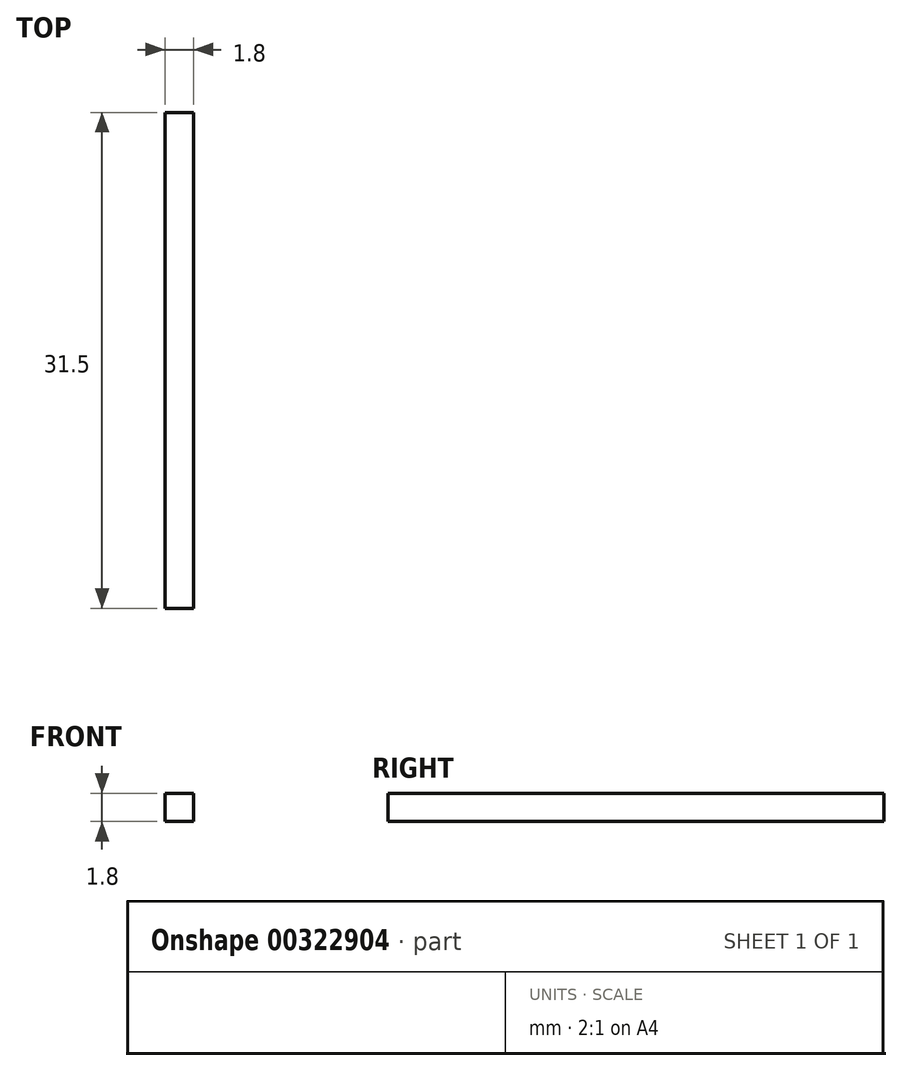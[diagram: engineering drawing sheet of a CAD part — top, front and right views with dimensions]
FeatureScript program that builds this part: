
annotation { "Feature Type Name" : "Feature", "Feature Type Description" : "" }
export const myFeature = defineFeature(function(context is Context, id is Id, definition is map)
    precondition{}
    {
        {
            var Q0;
            Q0=qCreatedBy(makeId("Front.planeOp"),FACE);
            var sketch = newSketch(context, id + "F0", { "sketchPlane" : qUnion([Q0])});
            skLineSegment(sketch, "E0.bottom", {"start": v(2.38, 2.38) * mm, "end": v(-2.37, 2.38) * mm});
            skLineSegment(sketch, "E0.top", {"start": v(2.37, -2.37) * mm, "end": v(-2.38, -2.37) * mm});
            skLineSegment(sketch, "E0.left", {"start": v(2.38, 2.38) * mm, "end": v(2.37, -2.37) * mm});
            skLineSegment(sketch, "E0.right", {"start": v(-2.37, 2.38) * mm, "end": v(-2.38, -2.37) * mm});
            skPoint(sketch, "E0.middle", {"position": v(0, 0) * mm});
            skLineSegment(sketch, "E1.bottom", {"start": v(0.9, 2.38) * mm, "end": v(-0.9, 2.38) * mm});
            skLineSegment(sketch, "E1.top", {"start": v(0.9, -2.38) * mm, "end": v(-0.9, -2.38) * mm});
            skLineSegment(sketch, "E1.left", {"start": v(0.9, 2.38) * mm, "end": v(0.9, -2.38) * mm});
            skLineSegment(sketch, "E1.right", {"start": v(-0.9, 2.38) * mm, "end": v(-0.9, -2.38) * mm});
            skLineSegment(sketch, "E2.bottom", {"start": v(2.38, 0.9) * mm, "end": v(-2.38, 0.9) * mm});
            skLineSegment(sketch, "E2.top", {"start": v(2.38, -0.9) * mm, "end": v(-2.38, -0.9) * mm});
            skLineSegment(sketch, "E2.left", {"start": v(2.38, 0.9) * mm, "end": v(2.38, -0.9) * mm});
            skLineSegment(sketch, "E2.right", {"start": v(-2.38, 0.9) * mm, "end": v(-2.38, -0.9) * mm});
            skSolve(sketch);
        }
        {
            var Q0;
            {var subQ0=sQuery(id+"F0.wireOp",EDGE,"E2.bottom");var subQ1=sQuery(id+"F0.wireOp",EDGE,"E1.left");var subQ2=makeQuery(id+"F0.imprint","INTERSECT",VERTEX,{"derivedFrom":[subQ1,subQ0]});Q0=makeQuery(id+"F0.imprint","IMPRINT",FACE,{"disambiguationData":[TD([[makeQuery(id+"F0.imprint","IMPRINT",EDGE,{"disambiguationData":[TD([[subQ2,-1.0]])],"derivedFrom":subQ1}),-1.0]])]});}
            var Q1;
            {var subQ5=sQuery(id+"F0.wireOp",EDGE,"E2.right");Q1=makeQuery(id+"F0.imprint","IMPRINT",FACE,{"disambiguationData":[TD([[makeQuery(id+"F0.imprint","IMPRINT",EDGE,{"derivedFrom":subQ5}),1.0]])]});}
            var Q2;
            {var subQ0=sQuery(id+"F0.wireOp",EDGE,"E1.bottom");Q2=makeQuery(id+"F0.imprint","IMPRINT",FACE,{"disambiguationData":[TD([[makeQuery(id+"F0.imprint","IMPRINT",EDGE,{"derivedFrom":subQ0}),1.0]])]});}
            var Q3;
            {var subQ0=sQuery(id+"F0.wireOp",EDGE,"E1.top");Q3=makeQuery(id+"F0.imprint","IMPRINT",FACE,{"disambiguationData":[TD([[makeQuery(id+"F0.imprint","IMPRINT",EDGE,{"derivedFrom":subQ0}),-1.0]])]});}
            var Q4;
            {var subQ5=sQuery(id+"F0.wireOp",EDGE,"E2.left");Q4=makeQuery(id+"F0.imprint","IMPRINT",FACE,{"disambiguationData":[TD([[makeQuery(id+"F0.imprint","IMPRINT",EDGE,{"derivedFrom":subQ5}),-1.0]])]});}
            extrude(context, id + "F1", {"entities" : qUnion([Q0, Q1, Q2, Q3, Q4]), "depth" : 31.5 * mm});
        }
    });
